# Revit family: EKF_EE_КомплектУсиленияFORT_PROxima
name_source: partatom
category: Электрооборудование
units: mm (PartAtom-declared; Revit-internal decimal feet)

## family parameters
Всегда вертикально = Нет
На основе рабочей плоскости = Да
Общий = Да
При загрузке вырезать с полостями = Нет
Размер круглого соединителя = Использовать диаметр
Тип детали = Силовой щит
Точка расчета площади = Нет

## types (1)
- Комплект усиления FORT EKF PROxima
    ADSK_Единица измерения = шт.
    ADSK_Завод-изготовитель = EKF
    ADSK_Код изделия = FKS8
    ADSK_Количество = 1
    ADSK_Марка = Комплект усиления FORT
    ADSK_Масса = 0
    ADSK_Материал = Сталь, с порошковым покрытием, белый
    ADSK_Наименование = Комплект усиления FORT EKF PROxima
    ADSK_Обозначение = Комплект усиления FORT
    t = 3 мм
    Высота = 74 мм
    Глубина = 98.5 мм
    Изготовитель = EKF
    Отметка по умолчанию = 0 мм
    Серия номенклатуры = PROxima
    Степень защиты IP = -
    ТВ = EKF_2
    Тип = 347 мм
    Тип установки = -
    Ширина = 84 мм
